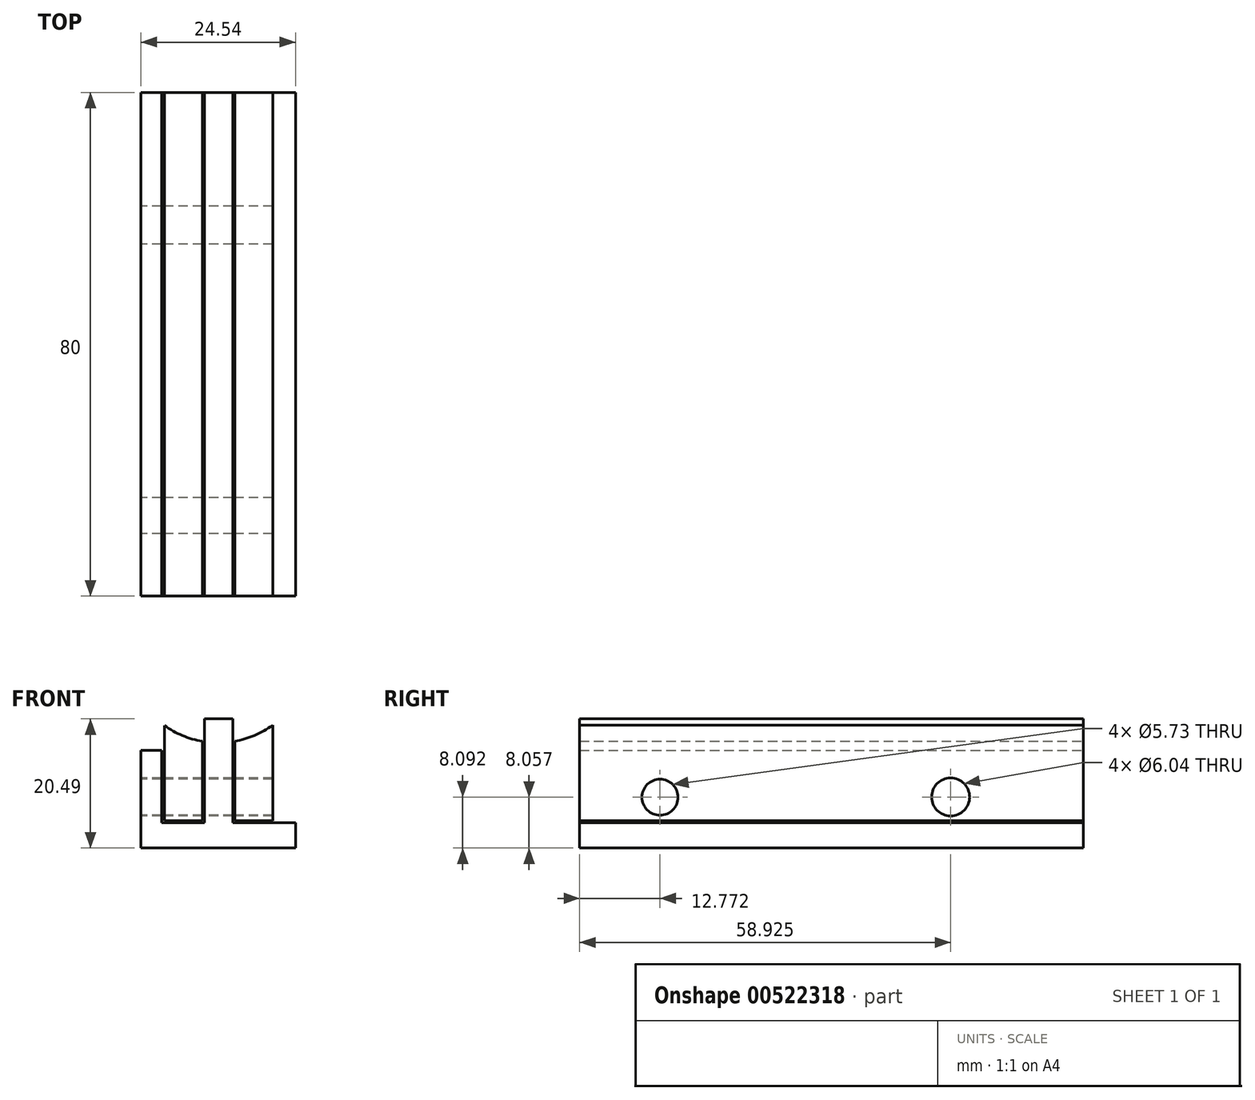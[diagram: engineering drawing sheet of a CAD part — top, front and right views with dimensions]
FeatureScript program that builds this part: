
annotation { "Feature Type Name" : "Feature", "Feature Type Description" : "" }
export const myFeature = defineFeature(function(context is Context, id is Id, definition is map)
    precondition{}
    {
        {
            var Q0;
            Q0=qCreatedBy(makeId("Front.planeOp"),FACE);
            var sketch = newSketch(context, id + "F0", { "sketchPlane" : qUnion([Q0])});
            skArc(sketch, "E0", {"start": v(0.05, 11.23) * mm, "mid": v(-11.15, 1.3) * mm, "end": v(-2.52, -10.94) * mm});
            skArc(sketch, "E1", {"start": v(0.05, 14.71) * mm, "mid": v(-14.66, 1.29) * mm, "end": v(-2.52, -14.5) * mm});
            skArc(sketch, "E2.MirrorCS", {"start": v(0.05, 11.25) * mm, "mid": v(11.17, 1.3) * mm, "end": v(2.62, -10.94) * mm});
            skArc(sketch, "E3.MirrorCS", {"start": v(0.05, 14.73) * mm, "mid": v(14.67, 1.3) * mm, "end": v(2.62, -14.5) * mm});
            skLineSegment(sketch, "E4.top", {"start": v(-2.52, -27.08) * mm, "end": v(-8.55, -27.08) * mm});
            skLineSegment(sketch, "E4.left", {"start": v(-2.52, -10.94) * mm, "end": v(-2.52, -27.08) * mm});
            skLineSegment(sketch, "E4.right", {"start": v(-8.55, -10.94) * mm, "end": v(-8.55, -27.08) * mm});
            skLineSegment(sketch, "E5.MirrorCS", {"start": v(2.62, -27.08) * mm, "end": v(8.65, -27.08) * mm});
            skLineSegment(sketch, "E6.MirrorCS", {"start": v(8.65, -10.94) * mm, "end": v(8.65, -27.08) * mm});
            skLineSegment(sketch, "E7.MirrorCS", {"start": v(2.62, -10.94) * mm, "end": v(2.62, -27.08) * mm});
            skCircle(sketch, "E8", {"center": v(0, 0) * mm, "radius": 11.28 * mm, "construction": true});
            skCircle(sketch, "E9", {"center": v(0, 0) * mm, "radius": 14.74 * mm, "construction": true});
            skLineSegment(sketch, "E10", {"start": v(-8.55, -12) * mm, "end": v(-8.55, -27.08) * mm, "construction": true});
            skLineSegment(sketch, "E11", {"start": v(-2.52, -27.08) * mm, "end": v(-2.52, -10.94) * mm, "construction": true});
            skLineSegment(sketch, "E12", {"start": v(2.62, -10.94) * mm, "end": v(2.62, -27.08) * mm, "construction": true});
            skLineSegment(sketch, "E13", {"start": v(8.65, -27.08) * mm, "end": v(8.65, -10.94) * mm, "construction": true});
            skSolve(sketch);
        }
        {
            var Q0;
            Q0=qCreatedBy(makeId("Front.planeOp"),FACE);
            var sketch = newSketch(context, id + "F1", { "sketchPlane" : qUnion([Q0])});
            skLineSegment(sketch, "E14.bottom", {"start": v(-2.2, -10.94) * mm, "end": v(2.33, -10.94) * mm});
            skLineSegment(sketch, "E14.top", {"start": v(-2.2, -31.55) * mm, "end": v(2.33, -31.55) * mm});
            skLineSegment(sketch, "E14.left", {"start": v(-2.2, -10.94) * mm, "end": v(-2.2, -31.55) * mm});
            skLineSegment(sketch, "E14.right", {"start": v(2.33, -10.94) * mm, "end": v(2.33, -31.55) * mm});
            skLineSegment(sketch, "E15.bottom", {"start": v(-12.27, -27.4) * mm, "end": v(12.27, -27.4) * mm});
            skLineSegment(sketch, "E15.top", {"start": v(-12.27, -39.43) * mm, "end": v(12.27, -39.43) * mm});
            skLineSegment(sketch, "E15.left", {"start": v(-12.27, -27.4) * mm, "end": v(-12.27, -39.43) * mm});
            skLineSegment(sketch, "E15.right", {"start": v(12.27, -27.4) * mm, "end": v(12.27, -39.43) * mm});
            skPoint(sketch, "E15.middle", {"position": v(0, -33.42) * mm});
            skLineSegment(sketch, "E16.bottom", {"start": v(12.27, -27.4) * mm, "end": v(9, -27.4) * mm});
            skLineSegment(sketch, "E16.top", {"start": v(12.27, -15.9) * mm, "end": v(9, -15.9) * mm});
            skLineSegment(sketch, "E16.left", {"start": v(12.27, -27.4) * mm, "end": v(12.27, -15.9) * mm});
            skLineSegment(sketch, "E16.right", {"start": v(9, -27.4) * mm, "end": v(9, -15.9) * mm});
            skLineSegment(sketch, "E17.MirrorCS", {"start": v(-12.27, -27.4) * mm, "end": v(-12.27, -15.9) * mm});
            skLineSegment(sketch, "E18.MirrorCS", {"start": v(-12.27, -27.4) * mm, "end": v(-9, -27.4) * mm});
            skLineSegment(sketch, "E19.MirrorCS", {"start": v(-9, -27.4) * mm, "end": v(-9, -15.9) * mm});
            skLineSegment(sketch, "E20.MirrorCS", {"start": v(-12.27, -15.9) * mm, "end": v(-9, -15.9) * mm});
            skSolve(sketch);
        }
        {
            var Q0;
            Q0=makeQuery(id+"F1.imprint","IMPRINT",FACE,{"disambiguationData":[TD([[makeQuery(id+"F1.imprint","IMPRINT",EDGE,{"derivedFrom":sQuery(id+"F1.wireOp",EDGE,"E16.bottom")}),-1.0]])]});
            var Q1;
            {var subQ5=sQuery(id+"F0.wireOp",EDGE,"E5.MirrorCS");Q1=makeQuery(id+"F0.imprint","IMPRINT",FACE,{"disambiguationData":[TD([[makeQuery(id+"F0.imprint","IMPRINT",EDGE,{"derivedFrom":subQ5}),1.0]])]});}
            var Q2;
            Q2=makeQuery(id+"F1.imprint","IMPRINT",FACE,{"disambiguationData":[TD([[makeQuery(id+"F1.imprint","IMPRINT",EDGE,{"derivedFrom":sQuery(id+"F1.wireOp",EDGE,"E17.MirrorCS")}),-1.0]])]});
            var Q3;
            {var subQ5=sQuery(id+"F0.wireOp",EDGE,"E4.top");Q3=makeQuery(id+"F0.imprint","IMPRINT",FACE,{"disambiguationData":[TD([[makeQuery(id+"F0.imprint","IMPRINT",EDGE,{"derivedFrom":subQ5}),-1.0]])]});}
            var Q4;
            {var subQ0=sQuery(id+"F1.wireOp",EDGE,"E14.top");Q4=makeQuery(id+"F1.imprint","IMPRINT",FACE,{"disambiguationData":[TD([[makeQuery(id+"F1.imprint","IMPRINT",EDGE,{"derivedFrom":subQ0}),1.0]])]});}
            var Q5;
            {var subQ0=sQuery(id+"F1.wireOp",EDGE,"E14.bottom");Q5=makeQuery(id+"F1.imprint","IMPRINT",FACE,{"disambiguationData":[TD([[makeQuery(id+"F1.imprint","IMPRINT",EDGE,{"derivedFrom":subQ0}),-1.0]])]});}
            var Q6;
            {var subQ1=sQuery(id+"F1.wireOp",EDGE,"E14.top");Q6=makeQuery(id+"F1.imprint","IMPRINT",FACE,{"disambiguationData":[TD([[makeQuery(id+"F1.imprint","IMPRINT",EDGE,{"derivedFrom":subQ1}),-1.0]])]});}
            extrude(context, id + "F2", {"entities" : qUnion([Q0, Q1, Q2, Q3, Q4, Q5, Q6]), "depth" : 80 * mm, "offsetDistance" : 25 * mm});
        }
        {
            var Q0;
            Q0=makeQuery(id+"F2.opExtrude","SWEPT_FACE",FACE,{"disambiguationData":[OSD([sQuery(id+"F1.wireOp",EDGE,"E15.left"),sQuery(id+"F1.wireOp",EDGE,"E17.MirrorCS")])]});
            var sketch = newSketch(context, id + "F3", { "sketchPlane" : qUnion([Q0])});
            skLineSegment(sketch, "E21.bottom", {"start": v(-41.43, 7.5) * mm, "end": v(38.28, 7.5) * mm, "construction": true});
            skLineSegment(sketch, "E21.top", {"start": v(-41.43, -7.53) * mm, "end": v(38.28, -7.53) * mm, "construction": true});
            skLineSegment(sketch, "E21.left", {"start": v(-41.43, 7.5) * mm, "end": v(-41.43, -7.53) * mm, "construction": true});
            skLineSegment(sketch, "E21.right", {"start": v(38.28, 7.5) * mm, "end": v(38.28, -7.53) * mm, "construction": true});
            skCircle(sketch, "E22", {"center": v(-20.35, 0.04) * mm, "radius": 3.14 * mm, "construction": true});
            skCircle(sketch, "E23", {"center": v(25.8, 0) * mm, "radius": 2.8 * mm, "construction": true});
            skCircle(sketch, "E24", {"center": v(-20.35, 0.04) * mm, "radius": 3.02 * mm});
            skCircle(sketch, "E25", {"center": v(25.8, 0) * mm, "radius": 2.87 * mm});
            skLineSegment(sketch, "E26.bottom", {"start": v(-41.43, 7.5) * mm, "end": v(39.13, 7.5) * mm});
            skLineSegment(sketch, "E26.top", {"start": v(-41.43, -7.53) * mm, "end": v(39.13, -7.53) * mm});
            skLineSegment(sketch, "E26.left", {"start": v(-41.43, 7.5) * mm, "end": v(-41.43, -7.53) * mm});
            skLineSegment(sketch, "E26.right", {"start": v(39.13, 7.5) * mm, "end": v(39.13, -7.53) * mm});
            skLineSegment(sketch, "E27.bottom", {"start": v(0, -15.87) * mm, "end": v(79.7, -15.87) * mm, "construction": true});
            skLineSegment(sketch, "E27.top", {"start": v(0, -30.9) * mm, "end": v(79.7, -30.9) * mm, "construction": true});
            skLineSegment(sketch, "E27.left", {"start": v(0, -15.87) * mm, "end": v(0, -30.9) * mm, "construction": true});
            skLineSegment(sketch, "E27.right", {"start": v(79.7, -15.87) * mm, "end": v(79.7, -30.9) * mm, "construction": true});
            skCircle(sketch, "E28", {"center": v(21.08, -23.33) * mm, "radius": 3.14 * mm, "construction": true});
            skCircle(sketch, "E29", {"center": v(67.23, -23.37) * mm, "radius": 2.8 * mm, "construction": true});
            skCircle(sketch, "E30", {"center": v(21.08, -23.33) * mm, "radius": 3.02 * mm});
            skCircle(sketch, "E31", {"center": v(67.23, -23.37) * mm, "radius": 2.87 * mm});
            skLineSegment(sketch, "E32.bottom", {"start": v(0, -15.87) * mm, "end": v(80.55, -15.87) * mm});
            skLineSegment(sketch, "E32.top", {"start": v(0, -30.9) * mm, "end": v(80.55, -30.9) * mm});
            skLineSegment(sketch, "E32.left", {"start": v(0, -15.87) * mm, "end": v(0, -30.9) * mm});
            skLineSegment(sketch, "E32.right", {"start": v(80.55, -15.87) * mm, "end": v(80.55, -30.9) * mm});
            skSolve(sketch);
        }
        {
            var Q0;
            {var subQ0=sQuery(id+"F1.wireOp",EDGE,"E15.left");Q0=makeQuery(id+"F3.imprint","IMPRINT",FACE,{"disambiguationData":[TD([[makeQuery(id+"F3.imprint","IMPRINT",EDGE,{"derivedFrom":makeQuery(id+"F2.opExtrude","SWEPT_EDGE",EDGE,{"disambiguationData":[OSD([sQuery(id+"F1.wireOp",EDGE,"E15.top"),subQ0])]})}),-1.0]])]});}
            var sketch = newSketch(context, id + "F4", { "sketchPlane" : qUnion([Q0])});
            skCircle(sketch, "E33", {"center": v(12.48, -23.91) * mm, "radius": 2.87 * mm});
            skPoint(sketch, "E33.first.point", {"position": v(12.36, -21.04) * mm});
            skPoint(sketch, "E33.second.point", {"position": v(10.26, -25.73) * mm});
            skPoint(sketch, "E33.third.point", {"position": v(15.05, -25.19) * mm});
            skCircle(sketch, "E34", {"center": v(58.62, -23.89) * mm, "radius": 3.02 * mm});
            skPoint(sketch, "E34.first.point", {"position": v(58.6, -20.87) * mm});
            skPoint(sketch, "E34.second.point", {"position": v(56.25, -25.78) * mm});
            skPoint(sketch, "E34.third.point", {"position": v(61.35, -25.19) * mm});
            skSolve(sketch);
        }
        {
            var Q0;
            {var subQ0=sQuery(id+"F1.wireOp",EDGE,"E15.left");Q0=makeQuery(id+"F3.imprint","IMPRINT",FACE,{"disambiguationData":[TD([[makeQuery(id+"F3.imprint","IMPRINT",EDGE,{"derivedFrom":makeQuery(id+"F2.opExtrude","SWEPT_EDGE",EDGE,{"disambiguationData":[OSD([sQuery(id+"F1.wireOp",EDGE,"E15.top"),subQ0])]})}),-1.0]])]});}
            var sketch = newSketch(context, id + "F5", { "sketchPlane" : qUnion([Q0])});
            skLineSegment(sketch, "E35.bottom", {"start": v(0, -15.88) * mm, "end": v(79.7, -15.88) * mm, "construction": true});
            skLineSegment(sketch, "E35.top", {"start": v(0, -30.9) * mm, "end": v(79.7, -30.9) * mm, "construction": true});
            skLineSegment(sketch, "E35.left", {"start": v(0, -15.88) * mm, "end": v(0, -30.9) * mm, "construction": true});
            skLineSegment(sketch, "E35.right", {"start": v(79.7, -15.88) * mm, "end": v(79.7, -30.9) * mm, "construction": true});
            skCircle(sketch, "E36", {"center": v(21.08, -23.34) * mm, "radius": 3.14 * mm, "construction": true});
            skCircle(sketch, "E37", {"center": v(67.23, -23.37) * mm, "radius": 2.8 * mm, "construction": true});
            skCircle(sketch, "E38", {"center": v(21.08, -23.34) * mm, "radius": 3.02 * mm});
            skCircle(sketch, "E39", {"center": v(67.23, -23.37) * mm, "radius": 2.87 * mm});
            skLineSegment(sketch, "E40.bottom", {"start": v(0, -15.88) * mm, "end": v(80.55, -15.88) * mm});
            skLineSegment(sketch, "E40.top", {"start": v(0, -30.9) * mm, "end": v(80.55, -30.9) * mm});
            skLineSegment(sketch, "E40.left", {"start": v(0, -15.88) * mm, "end": v(0, -30.9) * mm});
            skLineSegment(sketch, "E40.right", {"start": v(80.55, -15.88) * mm, "end": v(80.55, -30.9) * mm});
            skSolve(sketch);
        }
        {
            var Q0;
            Q0=makeQuery(id+"F5.imprint","IMPRINT",FACE,{"disambiguationData":[TD([[makeQuery(id+"F5.imprint","IMPRINT",EDGE,{"derivedFrom":sQuery(id+"F5.wireOp",EDGE,"E38")}),1.0]])]});
            var Q1;
            Q1=makeQuery(id+"F5.imprint","IMPRINT",FACE,{"disambiguationData":[TD([[makeQuery(id+"F5.imprint","IMPRINT",EDGE,{"derivedFrom":sQuery(id+"F5.wireOp",EDGE,"E39")}),1.0]])]});
            extrude(context, id + "F6", {"entities" : qUnion([Q0, Q1]), "operationType" : NewBodyOperationType.REMOVE, "oppositeDirection" : true, "depth" : 77 * mm, "offsetDistance" : 25 * mm});
        }
        {
            var Q0;
            Q0=makeQuery(id+"F2.opExtrude","SWEPT_FACE",FACE,{"disambiguationData":[OSD([sQuery(id+"F1.wireOp",EDGE,"E15.top")])]});
            extrude(context, id + "F7", {"entities" : qUnion([Q0]), "operationType" : NewBodyOperationType.ADD, "oppositeDirection" : true, "depth" : 9 * mm, "offsetDistance" : 25 * mm});
        }
        {
            var Q0;
            Q0=makeQuery(id+"F2.opExtrude","SWEPT_FACE",FACE,{"disambiguationData":[OSD([sQuery(id+"F1.wireOp",EDGE,"E15.top")])]});
            extrude(context, id + "F8", {"entities" : qUnion([Q0]), "operationType" : NewBodyOperationType.REMOVE, "oppositeDirection" : true, "depth" : 8 * mm, "offsetDistance" : 25 * mm});
        }
    });
